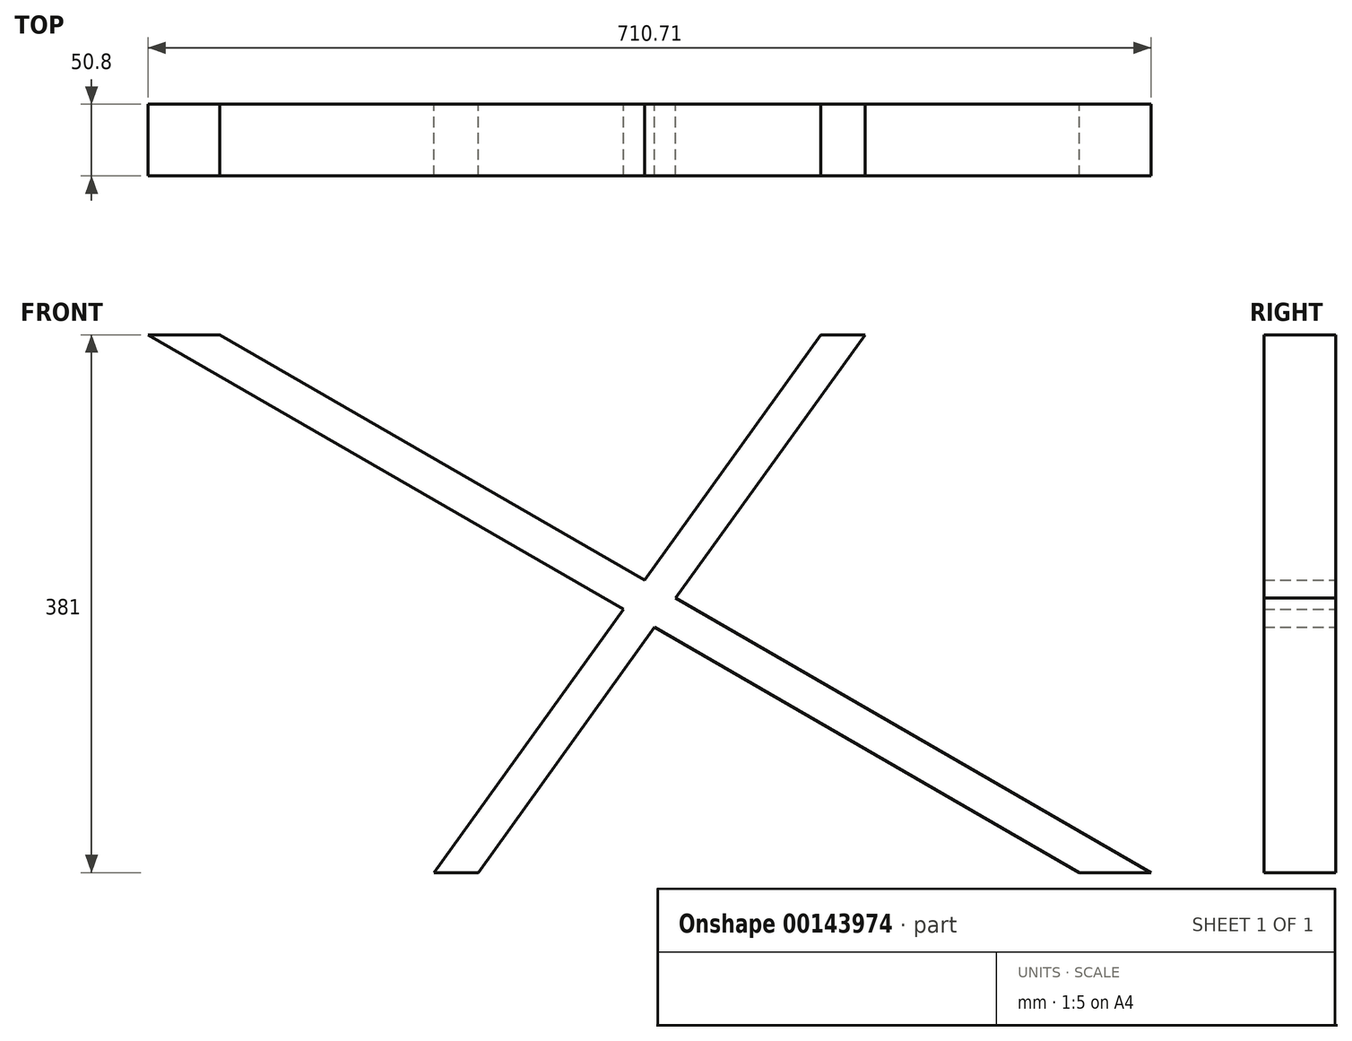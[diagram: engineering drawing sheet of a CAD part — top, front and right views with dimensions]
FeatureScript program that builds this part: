
annotation { "Feature Type Name" : "Feature", "Feature Type Description" : "" }
export const myFeature = defineFeature(function(context is Context, id is Id, definition is map)
    precondition{}
    {
        {
            var Q0;
            Q0=qCreatedBy(makeId("Front.planeOp"),FACE);
            var sketch = newSketch(context, id + "F0", { "sketchPlane" : qUnion([Q0])});
            skLineSegment(sketch, "E0.bottom", {"start": v(0, 0) * mm, "end": v(31.29, 0) * mm});
            skLineSegment(sketch, "E0.top", {"start": v(-202.71, 381) * mm, "end": v(-151.91, 381) * mm});
            skLineSegment(sketch, "E1", {"start": v(-202.71, 381) * mm, "end": v(457.2, 0) * mm});
            skLineSegment(sketch, "E2", {"start": v(-151.91, 381) * mm, "end": v(508, 0) * mm});
            skLineSegment(sketch, "E3", {"start": v(305.29, 381) * mm, "end": v(31.29, 0) * mm});
            skLineSegment(sketch, "E4", {"start": v(31.29, 0) * mm, "end": v(0, 0) * mm});
            skLineSegment(sketch, "E5", {"start": v(0, 0) * mm, "end": v(274, 381) * mm});
            skLineSegment(sketch, "E6.trimOffspring", {"start": v(274, 381) * mm, "end": v(305.29, 381) * mm});
            skLineSegment(sketch, "E7.trimOffspring", {"start": v(457.2, 0) * mm, "end": v(508, 0) * mm});
            skSolve(sketch);
        }
        {
            var Q0;
            Q0 = qSketchRegion(id + "F0", true);
            extrude(context, id + "F1", {"entities" : qUnion([Q0]), "depth" : 50.8 * mm});
        }
    });
